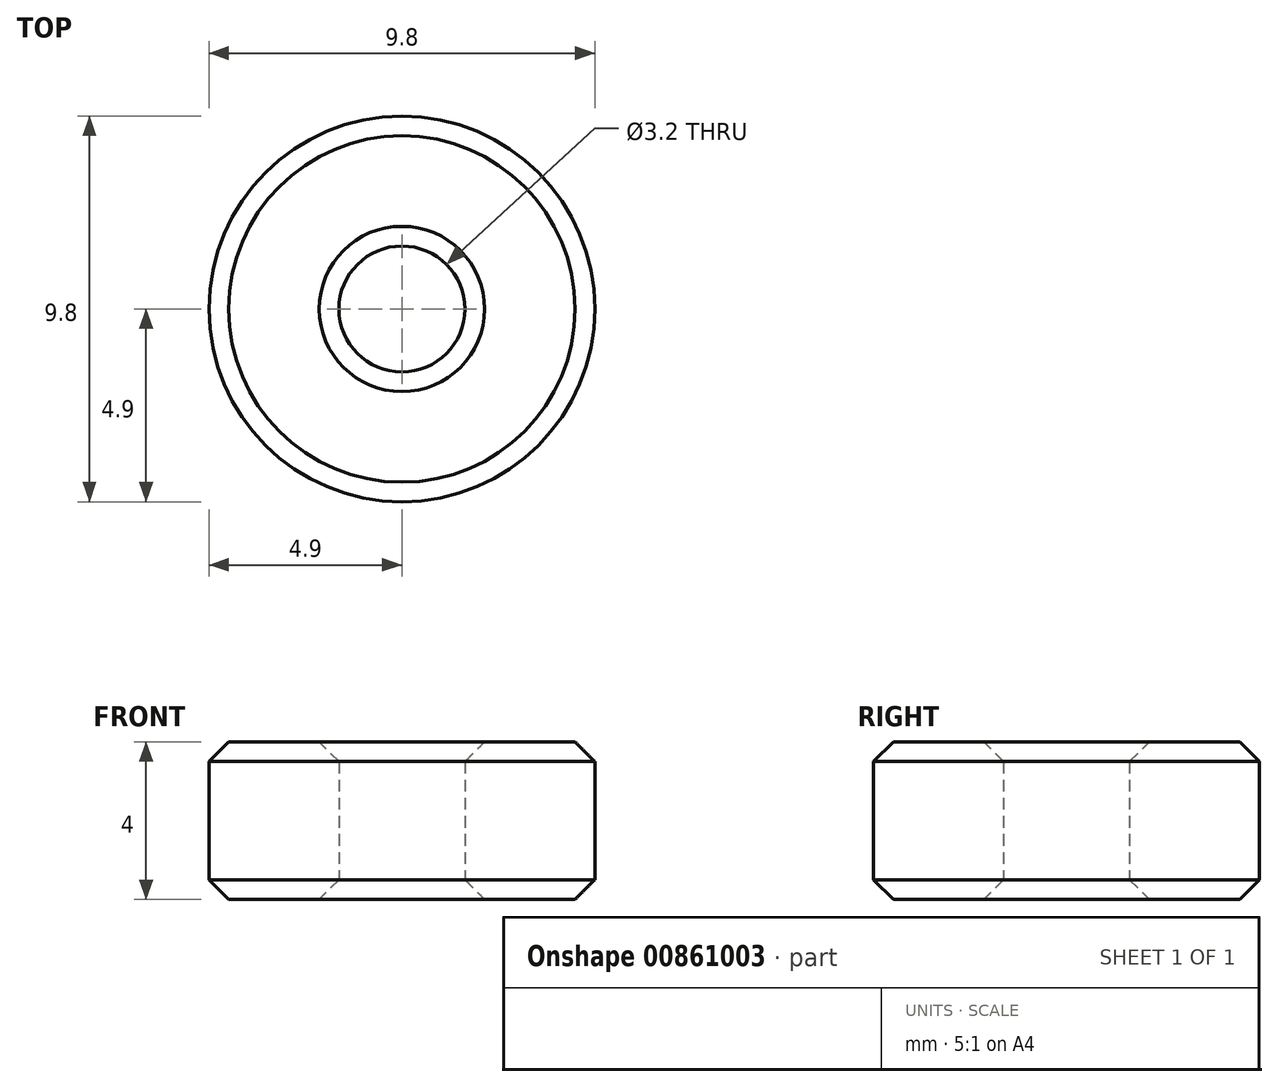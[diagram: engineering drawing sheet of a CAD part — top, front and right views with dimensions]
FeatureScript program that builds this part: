
annotation { "Feature Type Name" : "Feature", "Feature Type Description" : "" }
export const myFeature = defineFeature(function(context is Context, id is Id, definition is map)
    precondition{}
    {
        {
            var Q0;
            Q0=qCreatedBy(makeId("Top.planeOp"),FACE);
            var sketch = newSketch(context, id + "F0", { "sketchPlane" : qUnion([Q0])});
            skCircle(sketch, "E0", {"center": v(0, 0) * mm, "radius": 4.9 * mm});
            skCircle(sketch, "E1", {"center": v(0, 0) * mm, "radius": 1.6 * mm});
            skSolve(sketch);
        }
        {
            var Q0;
            Q0 = qSketchRegion(id + "F0", true);
            extrude(context, id + "F1", {"entities" : qUnion([Q0]), "depth" : 4 * mm, "offsetDistance" : 25 * mm});
        }
        {
            var Q0;
            Q0=makeQuery(id+"F1.opExtrude","CAP_FACE",FACE,{"disambiguationData":[OSD([sQuery(id+"F0.wireOp",EDGE,"E0"),sQuery(id+"F0.wireOp",EDGE,"E1")])],"isStart":false});
            var Q1;
            Q1=makeQuery(id+"F1.opExtrude","CAP_FACE",FACE,{"disambiguationData":[OSD([sQuery(id+"F0.wireOp",EDGE,"E0"),sQuery(id+"F0.wireOp",EDGE,"E1")])],"isStart":true});
            chamfer(context, id + "F2", {"entities" : qUnion([Q0, Q1]), "width" : 0.5 * mm, "tangentPropagation" : true});
        }
    });
